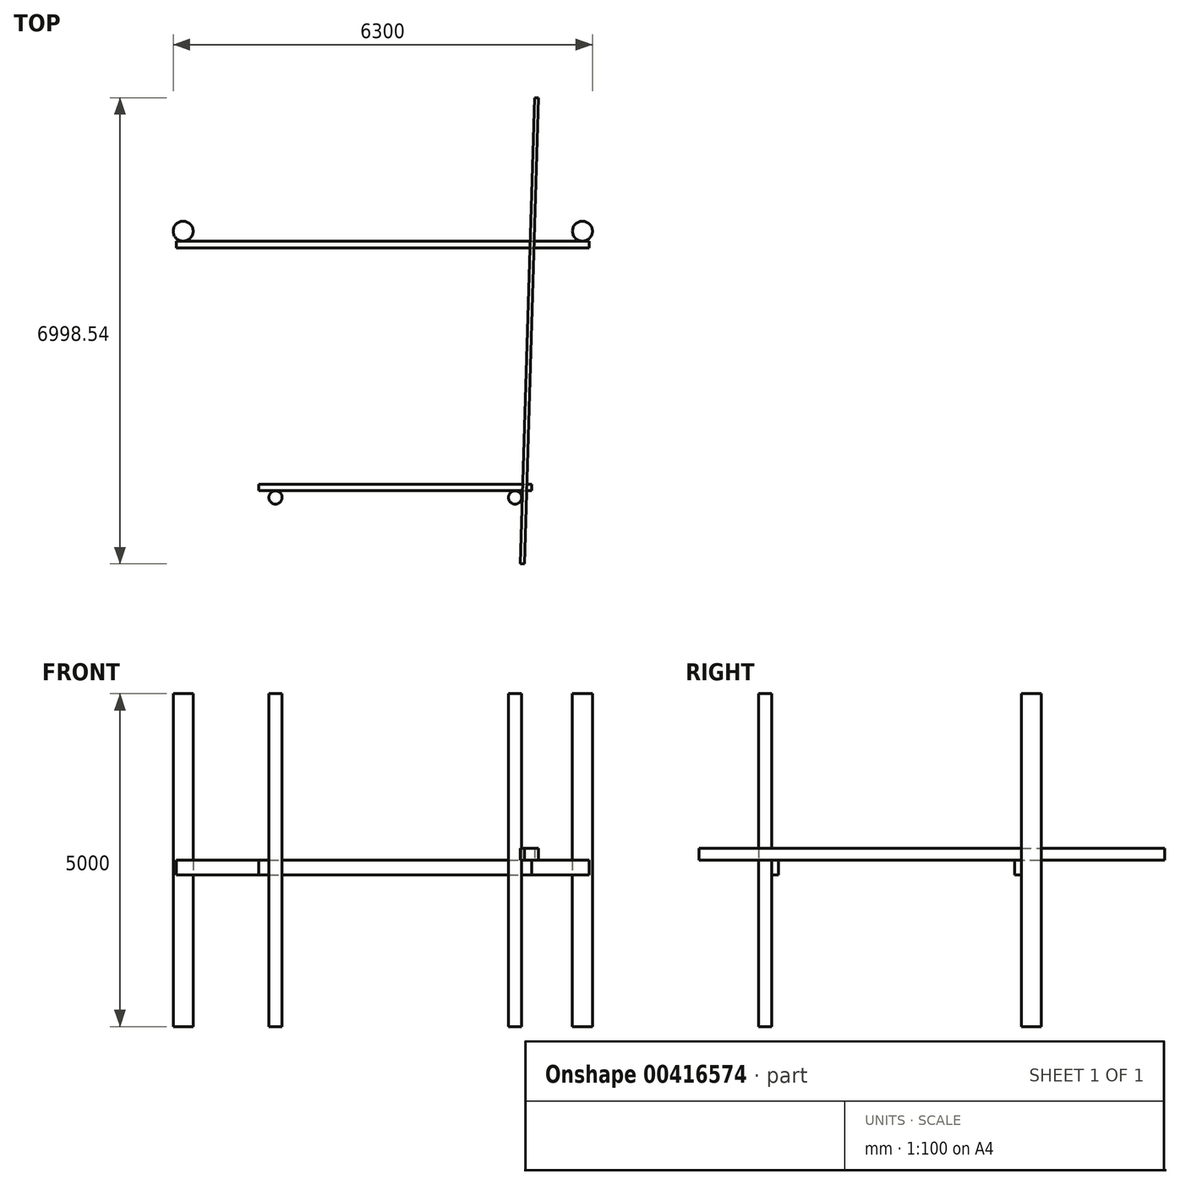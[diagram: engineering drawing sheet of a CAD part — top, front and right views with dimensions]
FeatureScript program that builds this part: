
annotation { "Feature Type Name" : "Feature", "Feature Type Description" : "" }
export const myFeature = defineFeature(function(context is Context, id is Id, definition is map)
    precondition{}
    {
        {
            var Q0;
            Q0=qCreatedBy(makeId("Top.planeOp"),FACE);
            var sketch = newSketch(context, id + "F0", { "sketchPlane" : qUnion([Q0])});
            skCircle(sketch, "E0", {"center": v(0, 0) * mm, "radius": 100 * mm});
            skCircle(sketch, "E1.0.1.0", {"center": v(-1387.21, 4000) * mm, "radius": 150 * mm});
            skCircle(sketch, "E1.1.0.0", {"center": v(3600, 0) * mm, "radius": 100 * mm});
            skCircle(sketch, "E1.1.1.0", {"center": v(4612.79, 4000) * mm, "radius": 150 * mm});
            skLineSegment(sketch, "E2", {"start": v(-1387.21, 4000) * mm, "end": v(4612.79, 4000) * mm, "construction": true});
            skLineSegment(sketch, "E3", {"start": v(3600, 0) * mm, "end": v(4612.79, 4000) * mm, "construction": true});
            skLineSegment(sketch, "E4", {"start": v(0, 0) * mm, "end": v(3600, 0) * mm, "construction": true});
            skLineSegment(sketch, "E5", {"start": v(-1387.21, 4000) * mm, "end": v(0, 0) * mm, "construction": true});
            skSolve(sketch);
        }
        {
            var Q0;
            Q0=makeQuery(id+"F0.imprint","IMPRINT",FACE,{"disambiguationData":[TD([[makeQuery(id+"F0.imprint","IMPRINT",EDGE,{"derivedFrom":sQuery(id+"F0.wireOp",EDGE,"E0")}),1.0]])]});
            var Q1;
            Q1=makeQuery(id+"F0.imprint","IMPRINT",FACE,{"disambiguationData":[TD([[makeQuery(id+"F0.imprint","IMPRINT",EDGE,{"derivedFrom":sQuery(id+"F0.wireOp",EDGE,"E1.0.1.0")}),1.0]])]});
            var Q2;
            Q2=makeQuery(id+"F0.imprint","IMPRINT",FACE,{"disambiguationData":[TD([[makeQuery(id+"F0.imprint","IMPRINT",EDGE,{"derivedFrom":sQuery(id+"F0.wireOp",EDGE,"E1.1.1.0")}),1.0]])]});
            var Q3;
            Q3=makeQuery(id+"F0.imprint","IMPRINT",FACE,{"disambiguationData":[TD([[makeQuery(id+"F0.imprint","IMPRINT",EDGE,{"derivedFrom":sQuery(id+"F0.wireOp",EDGE,"E1.1.0.0")}),1.0]])]});
            extrude(context, id + "F1", {"entities" : qUnion([Q0, Q1, Q2, Q3]), "depth" : 5000 * mm});
        }
        {
            var Q0;
            Q0=qCreatedBy(makeId("Top.planeOp"),FACE);
            var Q1;
            Q1=makeQuery(id+"F1.opExtrude","CAP_FACE",FACE,{"disambiguationData":[OSD([sQuery(id+"F0.wireOp",EDGE,"E1.0.1.0")])],"isStart":false});
            cPlane(context, id + "F2", {"entities" : qUnion([Q0, Q1]), "cplaneType" : CPlaneType.MID_PLANE, "offset" : 2820 * mm, "width" : 150 * mm, "height" : 150 * mm});
        }
        {
            var Q0;
            Q0=qCreatedBy(id+"F2.planeOp",FACE);
            var sketch = newSketch(context, id + "F3", { "sketchPlane" : qUnion([Q0])});
            skLineSegment(sketch, "E6", {"start": v(-737.21, 4000) * mm, "end": v(-140, 0) * mm, "construction": true});
            skLineSegment(sketch, "E7", {"start": v(-140, 0) * mm, "end": v(3740, 0) * mm});
            skLineSegment(sketch, "E8", {"start": v(3740, 0) * mm, "end": v(3862.79, 4000) * mm, "construction": true});
            skLineSegment(sketch, "E9", {"start": v(3862.79, 4000) * mm, "end": v(-737.21, 4000) * mm});
            skPoint(sketch, "E10", {"position": v(-737.21, 4000) * mm});
            skPoint(sketch, "E11.1.0.0", {"position": v(-383.36, 4000) * mm});
            skPoint(sketch, "E11.2.0.0", {"position": v(-29.52, 4000) * mm});
            skPoint(sketch, "E11.3.0.0", {"position": v(324.33, 4000) * mm});
            skPoint(sketch, "E11.4.0.0", {"position": v(678.17, 4000) * mm});
            skPoint(sketch, "E11.5.0.0", {"position": v(1032.02, 4000) * mm});
            skPoint(sketch, "E11.6.0.0", {"position": v(1385.87, 4000) * mm});
            skPoint(sketch, "E11.7.0.0", {"position": v(1739.71, 4000) * mm});
            skPoint(sketch, "E11.8.0.0", {"position": v(2093.56, 4000) * mm});
            skPoint(sketch, "E11.9.0.0", {"position": v(2447.4, 4000) * mm});
            skPoint(sketch, "E11.10.0.0", {"position": v(2801.25, 4000) * mm});
            skPoint(sketch, "E11.11.0.0", {"position": v(3155.1, 4000) * mm});
            skPoint(sketch, "E11.12.0.0", {"position": v(3508.94, 4000) * mm});
            skLineSegment(sketch, "E11.direction1", {"start": v(-737.21, 4000) * mm, "end": v(-383.36, 4000) * mm, "construction": true});
            skPoint(sketch, "E12", {"position": v(-140, 0) * mm});
            skPoint(sketch, "E13.1.0.0", {"position": v(158.46, 0) * mm});
            skPoint(sketch, "E13.2.0.0", {"position": v(456.92, 0) * mm});
            skPoint(sketch, "E13.3.0.0", {"position": v(755.38, 0) * mm});
            skPoint(sketch, "E13.4.0.0", {"position": v(1053.85, 0) * mm});
            skPoint(sketch, "E13.5.0.0", {"position": v(1352.3, 0) * mm});
            skPoint(sketch, "E13.6.0.0", {"position": v(1650.77, 0) * mm});
            skPoint(sketch, "E13.7.0.0", {"position": v(1949.23, 0) * mm});
            skPoint(sketch, "E13.8.0.0", {"position": v(2247.7, 0) * mm});
            skPoint(sketch, "E13.9.0.0", {"position": v(2546.15, 0) * mm});
            skPoint(sketch, "E13.10.0.0", {"position": v(2844.62, 0) * mm});
            skPoint(sketch, "E13.11.0.0", {"position": v(3143.08, 0) * mm});
            skPoint(sketch, "E13.12.0.0", {"position": v(3441.54, 0) * mm});
            skLineSegment(sketch, "E13.direction1", {"start": v(-140, 0) * mm, "end": v(158.46, 0) * mm, "construction": true});
            skLineSegment(sketch, "E14", {"start": v(-383.36, 4000) * mm, "end": v(158.46, 0) * mm, "construction": true});
            skLineSegment(sketch, "E15", {"start": v(456.92, 0) * mm, "end": v(-29.52, 4000) * mm, "construction": true});
            skLineSegment(sketch, "E16", {"start": v(324.33, 4000) * mm, "end": v(755.38, 0) * mm, "construction": true});
            skLineSegment(sketch, "E17", {"start": v(1053.85, 0) * mm, "end": v(678.17, 4000) * mm, "construction": true});
            skLineSegment(sketch, "E18", {"start": v(1032.02, 4000) * mm, "end": v(1352.3, 0) * mm, "construction": true});
            skLineSegment(sketch, "E19", {"start": v(1650.77, 0) * mm, "end": v(1385.87, 4000) * mm, "construction": true});
            skLineSegment(sketch, "E20", {"start": v(1739.71, 4000) * mm, "end": v(1949.23, 0) * mm, "construction": true});
            skLineSegment(sketch, "E21", {"start": v(2247.7, 0) * mm, "end": v(2093.56, 4000) * mm, "construction": true});
            skLineSegment(sketch, "E22", {"start": v(2447.4, 4000) * mm, "end": v(2546.15, 0) * mm, "construction": true});
            skLineSegment(sketch, "E23", {"start": v(2844.62, 0) * mm, "end": v(2801.25, 4000) * mm, "construction": true});
            skLineSegment(sketch, "E24", {"start": v(3155.1, 4000) * mm, "end": v(3143.08, 0) * mm, "construction": true});
            skLineSegment(sketch, "E25", {"start": v(3441.54, 0) * mm, "end": v(3508.94, 4000) * mm, "construction": true});
            skLineSegment(sketch, "E26", {"start": v(-1035.82, 6000) * mm, "end": v(3924.18, 6000) * mm, "construction": true});
            skSolve(sketch);
        }
        {
            var Q0;
            Q0=qCreatedBy(id+"F2.planeOp",FACE);
            var sketch = newSketch(context, id + "F4", { "sketchPlane" : qUnion([Q0])});
            skLineSegment(sketch, "E27.bottom", {"start": v(-250, 100) * mm, "end": v(3850, 100) * mm});
            skLineSegment(sketch, "E27.top", {"start": v(-250, 200) * mm, "end": v(3850, 200) * mm});
            skLineSegment(sketch, "E27.left", {"start": v(-250, 100) * mm, "end": v(-250, 200) * mm});
            skLineSegment(sketch, "E27.right", {"start": v(3850, 100) * mm, "end": v(3850, 200) * mm});
            skPoint(sketch, "E28", {"position": v(1800, 100) * mm});
            skSolve(sketch);
        }
        {
            var Q0;
            Q0=makeQuery(id+"F4.imprint","IMPRINT",FACE,{"disambiguationData":[TD([[makeQuery(id+"F4.imprint","IMPRINT",EDGE,{"derivedFrom":sQuery(id+"F4.wireOp",EDGE,"E27.bottom")}),1.0]])]});
            extrude(context, id + "F5", {"entities" : qUnion([Q0]), "operationType" : NewBodyOperationType.ADD, "oppositeDirection" : true, "depth" : 220 * mm});
        }
        {
            var Q0;
            Q0=qCreatedBy(id+"F2.planeOp",FACE);
            var sketch = newSketch(context, id + "F6", { "sketchPlane" : qUnion([Q0])});
            skLineSegment(sketch, "E29.bottom", {"start": v(-1487.21, 3750) * mm, "end": v(4712.79, 3750) * mm});
            skLineSegment(sketch, "E29.top", {"start": v(-1487.21, 3850) * mm, "end": v(4712.79, 3850) * mm});
            skLineSegment(sketch, "E29.left", {"start": v(-1487.21, 3750) * mm, "end": v(-1487.21, 3850) * mm});
            skLineSegment(sketch, "E29.right", {"start": v(4712.79, 3750) * mm, "end": v(4712.79, 3850) * mm});
            skPoint(sketch, "E30", {"position": v(1612.79, 3850) * mm});
            skSolve(sketch);
        }
        {
            var Q0;
            Q0 = qSketchRegion(id + "F6", true);
            var Q1;
            Q1=makeQuery(id+"F5.opExtrude","CAP_FACE",FACE,{"disambiguationData":[OSD([sQuery(id+"F4.wireOp",EDGE,"E27.bottom"),sQuery(id+"F4.wireOp",EDGE,"E27.top"),sQuery(id+"F4.wireOp",EDGE,"E27.left"),sQuery(id+"F4.wireOp",EDGE,"E27.right")])],"isStart":false});
            extrude(context, id + "F7", {"entities" : qUnion([Q0]), "endBound" : BoundingType.UP_TO_SURFACE, "oppositeDirection" : true, "endBoundEntityFace" : qUnion([Q1]), "depth" : 25 * mm});
        }
        {
            var Q0;
            Q0=qCreatedBy(id+"F2.planeOp",FACE);
            var sketch = newSketch(context, id + "F8", { "sketchPlane" : qUnion([Q0])});
            skLineSegment(sketch, "E31.bottom", {"start": v(3679.46, -994.45) * mm, "end": v(3739.43, -996.3) * mm});
            skLineSegment(sketch, "E31.top", {"start": v(3894.24, 6002.25) * mm, "end": v(3954.21, 6000.41) * mm});
            skLineSegment(sketch, "E31.left", {"start": v(3679.46, -994.45) * mm, "end": v(3894.24, 6002.25) * mm});
            skLineSegment(sketch, "E31.right", {"start": v(3739.43, -996.3) * mm, "end": v(3954.21, 6000.41) * mm});
            skLineSegment(sketch, "E32", {"start": v(3924.23, 6001.33) * mm, "end": v(3709.44, -995.37) * mm, "construction": true});
            skSolve(sketch);
        }
        {
            var Q0;
            Q0=makeQuery(id+"F8.imprint","IMPRINT",FACE,{"disambiguationData":[TD([[makeQuery(id+"F8.imprint","IMPRINT",EDGE,{"derivedFrom":sQuery(id+"F8.wireOp",EDGE,"E31.bottom")}),1.0]])]});
            extrude(context, id + "F9", {"entities" : qUnion([Q0]), "depth" : 180 * mm});
        }
    });
